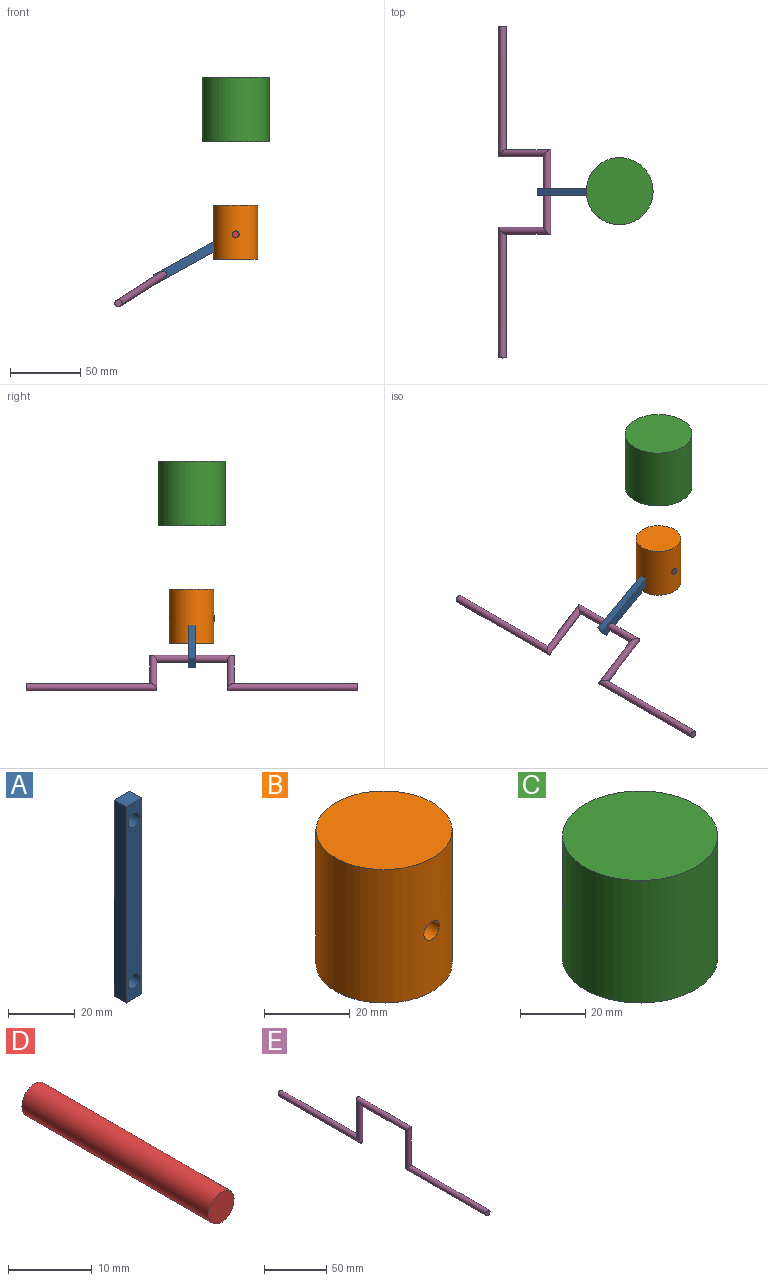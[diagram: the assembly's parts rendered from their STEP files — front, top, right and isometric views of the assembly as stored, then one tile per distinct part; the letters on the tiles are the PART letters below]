
ASSEMBLY  parts=5 mates=4
PART A: 8 faces, bbox 6.7x5.1x71.6 mm
  f0: plane 6.71x5.08mm, normal (0,0,1), area 34.1mm2, adj f1,f5,f6,f7
  f1: plane 71.62x5.08mm, normal (-1,0,0), area 363.8mm2, adj f0,f2,f6,f7
  f2: plane 6.71x5.08mm, normal (0,0,-1), area 34.1mm2, adj f1,f5,f6,f7
  f3: cylinder r=2.54mm len=5.08mm, axis (0,1,0), area 81.1mm2, adj f6,f7
  f4: cylinder r=2.54mm len=5.08mm, axis (0,1,0), area 81.1mm2, adj f6,f7
  f5: plane 71.62x5.08mm, normal (1,0,0), area 363.8mm2, adj f0,f2,f6,f7
  f6: plane 71.62x6.71mm, normal (0,-1,0), area 439.9mm2, adj f0,f1,f2,f3,f4,f5
  f7: plane 71.62x6.71mm, normal (0,1,0), area 439.9mm2, adj f0,f1,f2,f3,f4,f5
PART B: 10 faces, bbox 31.8x31.8x38.1 mm
  f0: plane 31.75x31.75mm, normal (0,0,-1), area 509.8mm2, adj f1,f4,f5,f6,f7
  f1: cylinder r=15.88mm len=38.1mm, axis (0,0,1), area 3759.9mm2, adj f0,f2,f8,f9
  f2: plane 31.75x31.75mm, normal (0,0,1), area 791.7mm2, adj f1
  f3: plane 21.59x13.06mm, normal (0,0,-1), area 281.9mm2, adj f4,f5,f6,f7
  f4: plane 25.4x13.06mm, normal (0,1,0), area 311.4mm2, adj f0,f3,f5,f7,f9
  f5: plane 25.4x21.59mm, normal (1,0,0), area 548.4mm2, adj f0,f3,f4,f6
  f6: plane 25.4x13.06mm, normal (0,-1,0), area 311.4mm2, adj f0,f3,f5,f7,f8
  f7: plane 25.4x21.59mm, normal (-1,0,0), area 548.4mm2, adj f0,f3,f4,f6
  f8: cylinder r=2.54mm len=5.08mm, axis (0,-1,0), area 79.4mm2, adj f1,f6
  f9: cylinder r=2.54mm len=5.08mm, axis (0,-1,0), area 79.4mm2, adj f1,f4
PART C: 5 faces, bbox 47.6x47.6x46 mm
  f0: plane 34.93x34.93mm, normal (0,0,-1), area 958mm2, adj f1
  f1: cylinder r=17.46mm len=39.69mm, axis (0,0,1), area 4354.5mm2, adj f0,f2
  f2: plane 47.63x47.63mm, normal (0,0,-1), area 823.4mm2, adj f1,f3
  f3: cylinder r=23.81mm len=47.63mm, axis (0,0,1), area 6888.1mm2, adj f2,f4
  f4: plane 47.63x47.63mm, normal (0,0,1), area 1781.4mm2, adj f3
PART D: 3 faces, bbox 4.4x31.8x4.4 mm
  f0: cylinder r=15.88mm len=4.4mm, axis (0,0,1), area 15.2mm2, adj f2
  f1: cylinder r=15.88mm len=4.4mm, axis (0,0,1), area 15.2mm2, adj f2
  f2: cylinder r=2.2mm len=31.75mm, axis (0,1,0), area 436.8mm2, adj f0,f1
PART E: 7 faces, bbox 5.1x236.1x42.8 mm
  f0: plane 5.08x5.08mm, normal (0,-1,0), area 20.3mm2, adj f2
  f1: plane 5.08x5.08mm, normal (0,1,0), area 20.3mm2, adj f6
  f2: cylinder r=2.54mm len=92.97mm, axis (0,-1,0), area 1443.2mm2, adj f0,f3
  f3: cylinder r=2.54mm len=42.83mm, axis (0,0,-1), area 602.4mm2, adj f2,f4
  f4: cylinder r=2.54mm len=60.35mm, axis (0,-1,0), area 882.1mm2, adj f3,f5
  f5: cylinder r=2.54mm len=42.83mm, axis (0,0,1), area 602.4mm2, adj f4,f6
  f6: cylinder r=2.54mm len=92.97mm, axis (0,-1,0), area 1443.2mm2, adj f1,f5
PLACE A rot(axis=(0,1,0),60.9deg) t=(-103.36,-41.38,-41.85)mm
PLACE B t=(-88.1,-41.07,-50.83)mm
PLACE C t=(-88.1,-41.07,32.53)mm fixed
PLACE D t=(-88.1,-41.38,-50.83)mm
PLACE E rot(axis=(0,1,0),57.4deg) t=(-104.67,-41.38,-39.64)mm
MATE revolute A.f3 <-> D.f2  axis (0,1,0) through (-88.1,-41.38,-33.36)mm
MATE slider B.f1 <-> C.f1  axis (0,0,1) through (-88.1,-41.07,-12.73)mm
MATE slider D.f2 <-> B.f8  axis (0,1,0) through (-88.1,-41.38,-33.36)mm
MATE revolute A.f4 <-> E.f4  axis (0,1,0) through (-139.6,-41.38,-61.98)mm
